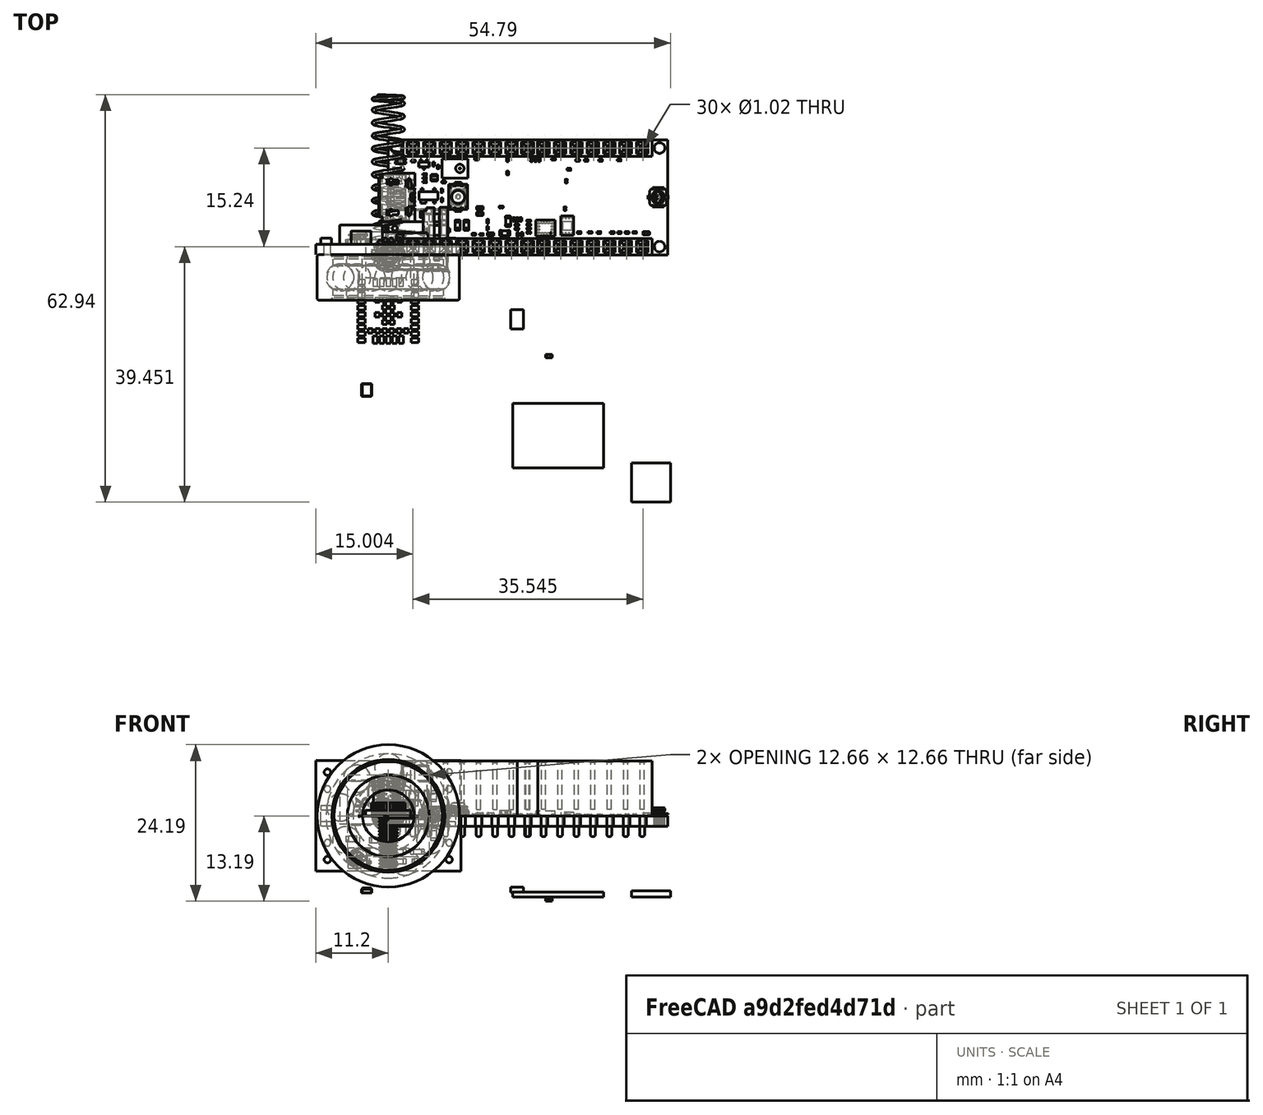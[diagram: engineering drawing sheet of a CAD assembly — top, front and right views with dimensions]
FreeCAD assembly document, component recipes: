
FREECAD ASSEMBLY — COMPONENT RECIPES ("Watch_Winder")

This assembly document has 14 components, labeled P0..P13 below (a component is one placed body or linked part). 4 of them carry a construction recipe — the FreeCAD feature program that regenerates the part from scratch, quoted from this document or its linked companion documents; the rest are supplied as boundary geometry only. No exploded tour is included for this assembly.
COMPONENT P0 — recipe-attached ("Bearing_Stopper001", modeled in this document).
Construction recipe (the document's own serialized feature program — sketch geometry with constraints, then the solid features built on it; lengths are millimeters unless a unit is written):

FEATURE [Sketcher::SketchObject] Sketch021
  ArcFitTolerance = 1e-06
  AttachmentSupport = -> [XZ_Plane150]
  FullyConstrained = true
  MakeInternals = false
  MapMode = 5
  Placement = pos=(0,0,0) rot=(1,0,0;1.5708rad)
  expr: Constraints[16] = 4.2 / 2
  sketch-geometry (6):
    g0: LineSegment StartX=0 StartY=-2.1 StartZ=0 EndX=0 EndY=-8 EndZ=0
    g1: LineSegment StartX=0 StartY=-8 StartZ=0 EndX=-3 EndY=-8 EndZ=0
    g2: LineSegment StartX=-3 StartY=-8 StartZ=0 EndX=-3 EndY=-4 EndZ=0
    g3: LineSegment StartX=-3 StartY=-4 StartZ=0 EndX=-10 EndY=-4 EndZ=0
    g4: LineSegment StartX=-10 StartY=-4 StartZ=0 EndX=-10 EndY=-2.1 EndZ=0
    g5: LineSegment StartX=-10 StartY=-2.1 StartZ=0 EndX=0 EndY=-2.1 EndZ=0
  constraints (18):
    c: PointOnObject(g0,g-2)
    c: Coincident(g1,g0)
    c: Horizontal(g1)
    c: Coincident(g2,g1)
    c: Vertical(g2)
    c: Coincident(g3,g2)
    c: Horizontal(g3)
    c: Coincident(g4,g3)
    c: Vertical(g4)
    c: DistanceX(g3,g3) = 7
    c: DistanceX(g1,g1) = 3
    c: Horizontal(g5)
    c: Coincident(g0,g5)
    c: Coincident(g4,g5)
    c: DistanceY(g3,g-1) = 4
    c: DistanceY(g0,g-1) = 8
    c: DistanceY(g4,g-1) = 2.1
    c: Vertical(g0)
FEATURE [PartDesign::Revolution] Revolution
  Angle = 360
  Angle2 = 60
  Axis = (1,0,0)
  Base = (0,0,0)
  Placement = pos=(0,0,0) rot=(1,0,0;1.5708rad)
  Profile = -> Sketch021
  ReferenceAxis = -> Sketch021 [H_Axis]
  Refine = true
  Reversed = true
  Suppressed = false
  Type = 0
FEATURE [PartDesign::Fillet] Fillet012
  Base = -> Revolution [Edge2]
  BaseFeature = -> Revolution
  Placement = pos=(0,0,0) rot=(1,0,0;1.5708rad)
  Radius = 1
  Refine = true
  SupportTransform = false
  Suppressed = false
  UseAllEdges = false
FEATURE [PartDesign::Body] Body006  label="Bearing_Stopper"
  AllowCompound = false
  Group = -> [Sketch021,Revolution,Fillet012]
  Origin = -> Origin150
  Placement = pos=(-21.5,25.5,-38) rot=(0,0,1;0rad)
  Tip = -> Fillet012
COMPONENT P1 — same part as P0; its construction recipe is shown at P0.
COMPONENT P2 — recipe-attached ("Body009", modeled in this document).
Construction recipe (the document's own serialized feature program — sketch geometry with constraints, then the solid features built on it; lengths are millimeters unless a unit is written):

FEATURE [Sketcher::SketchObject] Sketch011
  ArcFitTolerance = 1e-06
  AttachmentSupport = -> [YZ_Plane005]
  FullyConstrained = true
  MakeInternals = false
  MapMode = 5
  Placement = pos=(0,0,0) rot=(0.57735,0.57735,0.57735;2.0944rad)
  sketch-geometry (7):
    g0: LineSegment StartX=-67.5 StartY=55 StartZ=0 EndX=-67.5 EndY=-55 EndZ=0
    g1: LineSegment StartX=-67.5 StartY=-55 StartZ=0 EndX=42.5 EndY=-55 EndZ=0
    g2: LineSegment StartX=42.5 StartY=-55 StartZ=0 EndX=42.5 EndY=55 EndZ=0
    g3: LineSegment StartX=42.5 StartY=55 StartZ=0 EndX=-67.5 EndY=55 EndZ=0
    g4: LineSegment [constr] StartX=-12.5 StartY=55 StartZ=0 EndX=-12.5 EndY=-55 EndZ=0
    g5: LineSegment [constr] StartX=-67.5 StartY=-7e-16 StartZ=0 EndX=42.5 EndY=7e-16 EndZ=0
    g6: GeomPoint [constr] X=-12.5 Y=0 Z=0
  constraints (17):
    c: Coincident(g0,g1)
    c: Coincident(g1,g2)
    c: Coincident(g2,g3)
    c: Coincident(g3,g0)
    c: Vertical(g0)
    c: Vertical(g2)
    c: Horizontal(g1)
    c: Horizontal(g3)
    c: DistanceX(g3,g3) = 110
    c: DistanceY(g0,g0) = 110
    c: Symmetric(g3,g3,g4)
    c: Symmetric(g1,g1,g4)
    c: Symmetric(g0,g0,g5)
    c: Symmetric(g2,g2,g5)
    c: Symmetric(g5,g5,g6)
    c: DistanceX(g6,g-1) = 12.5
    c: PointOnObject(g6,g-1)
FEATURE [PartDesign::Pad] Pad006  label="Depth"
  Direction = (1,0,0)
  Length = 86
  Length2 = 10
  Placement = pos=(0,0,0) rot=(1,1,1;2.0944rad)
  Profile = -> Sketch011
  ReferenceAxis = -> Sketch011 [N_Axis]
  Refine = true
  Reversed = true
  Suppressed = false
  Type = 0
FEATURE [Sketcher::SketchObject] Sketch012
  ArcFitTolerance = 1e-06
  AttachmentSupport = -> [Pad006]
  ExternalGeometry = -> [Pad006]
  FullyConstrained = true
  MakeInternals = false
  MapMode = 5
  Placement = pos=(0,0,0) rot=(0.57735,0.57735,0.57735;2.0944rad)
  sketch-geometry (4):
    g0: LineSegment [constr] StartX=-67.5 StartY=2.15e-14 StartZ=0 EndX=42.5 EndY=-1.24e-14 EndZ=0
    g1: LineSegment [constr] StartX=-12.5 StartY=-55 StartZ=0 EndX=-12.5 EndY=55 EndZ=0
    g2: GeomPoint [constr] X=-12.5 Y=4.5e-15 Z=0
    g3: Circle CenterX=-12.5 CenterY=4.5e-15 CenterZ=0 NormalX=0 NormalY=0 NormalZ=1 AngleXU=0 Radius=44
  constraints (7):
    c: Symmetric(g-6,g-6,g0)
    c: Symmetric(g-5,g-5,g0)
    c: Symmetric(g-4,g-4,g1)
    c: Symmetric(g-3,g-3,g1)
    c: Symmetric(g0,g0,g2)
    c: Coincident(g3,g2)
    c: Diameter(g3) = 88
FEATURE [PartDesign::Pocket] Pocket005  label="Drum_Cavity"
  BaseFeature = -> Pad006
  Direction = (-1,0,0)
  Length = 58
  Length2 = 5
  Placement = pos=(0,0,0) rot=(1,1,1;2.0944rad)
  Profile = -> Sketch012
  ReferenceAxis = -> Sketch012 [N_Axis]
  Refine = true
  Suppressed = false
  Type = 0
FEATURE [Sketcher::SketchObject] Sketch013
  ArcFitTolerance = 1e-06
  AttachmentSupport = -> [Pocket005]
  ExternalGeometry = -> [Pocket005]
  FullyConstrained = true
  MakeInternals = false
  MapMode = 5
  Placement = pos=(0,0,0) rot=(0.57735,0.57735,0.57735;2.0944rad)
  expr: Constraints[4] = 85 / 2 + 22 / 2
  sketch-geometry (6):
    g0: LineSegment [constr] StartX=-12.5 StartY=8.7e-15 StartZ=0 EndX=42.5 EndY=-55 EndZ=0
    g1: Circle [constr] CenterX=25.3302 CenterY=-37.8302 CenterZ=0 NormalX=0 NormalY=0 NormalZ=1 AngleXU=0 Radius=11
    g2: Circle CenterX=25.3302 CenterY=-37.8302 CenterZ=0 NormalX=0 NormalY=0 NormalZ=1 AngleXU=0 Radius=11.75
    g3: LineSegment [constr] StartX=-12.5 StartY=8.7e-15 StartZ=0 EndX=-67.5 EndY=-55 EndZ=0
    g4: LineSegment [constr] StartX=25.3302 StartY=-37.8302 StartZ=0 EndX=-50.3302 EndY=-37.8302 EndZ=0
    g5: Circle CenterX=-50.3302 CenterY=-37.8302 CenterZ=0 NormalX=0 NormalY=0 NormalZ=1 AngleXU=0 Radius=11.75
  constraints (14):
    c: Coincident(g0,g-3)
    c: Coincident(g0,g-5)
    c: PointOnObject(g1,g0)
    c: Diameter(g1) = 22
    c: Distance(g1,g0) = 53.5
    c: Coincident(g2,g1)
    c: Coincident(g3,g0)
    c: Coincident(g3,g-6)
    c: Coincident(g4,g1)
    c: PointOnObject(g4,g3)
    c: Horizontal(g4)
    c: Coincident(g5,g4)
    c: Equal(g2,g5)
    c: Diameter(g2) = 23.5
FEATURE [PartDesign::Pocket] Pocket006  label="Bearing"
  BaseFeature = -> Pocket005
  Direction = (-1,0,0)
  Length = 31.5
  Length2 = 5
  Placement = pos=(0,0,0) rot=(1,1,1;2.0944rad)
  Profile = -> Sketch013
  ReferenceAxis = -> Sketch013 [N_Axis]
  Refine = true
  Suppressed = false
  Type = 0
  expr: Length = 56 / 2 + 7 / 2
FEATURE [Sketcher::SketchObject] Sketch016
  ArcFitTolerance = 1e-06
  AttachmentSupport = -> [Pocket006]
  ExternalGeometry = -> [Pocket006]
  FullyConstrained = true
  MakeInternals = false
  MapMode = 5
  Placement = pos=(-86,0,0) rot=(0.57735,0.57735,-0.57735;4.18879rad)
  expr: Constraints[20] = 90 - 35
  sketch-geometry (8):
    g0: LineSegment StartX=32.5 StartY=-45 StartZ=0 EndX=32.5 EndY=27 EndZ=0
    g1: LineSegment StartX=-22.5 StartY=45 StartZ=0 EndX=-57.5 EndY=45 EndZ=0
    g2: LineSegment StartX=-57.5 StartY=45 StartZ=0 EndX=-57.5 EndY=-45 EndZ=0
    g3: LineSegment StartX=-57.5 StartY=-45 StartZ=0 EndX=32.5 EndY=-45 EndZ=0
    g4: LineSegment [constr] StartX=-12.5 StartY=-55 StartZ=0 EndX=-12.5 EndY=55 EndZ=0
    g5: LineSegment [constr] StartX=42.5 StartY=4.18e-14 StartZ=0 EndX=-67.5 EndY=0 EndZ=0
    g6: LineSegment StartX=-22.5 StartY=27 StartZ=0 EndX=32.5 EndY=27 EndZ=0
    g7: LineSegment StartX=-22.5 StartY=27 StartZ=0 EndX=-22.5 EndY=45 EndZ=0
  constraints (22):
    c: Coincident(g1,g2)
    c: Coincident(g2,g3)
    c: Coincident(g3,g0)
    c: Vertical(g0)
    c: Vertical(g2)
    c: Horizontal(g1)
    c: Horizontal(g3)
    c: DistanceX(g3,g3) = 90
    c: Symmetric(g-3,g-3,g4)
    c: Symmetric(g-4,g-4,g4)
    c: DistanceX(g2,g4) = 45
    c: Symmetric(g-5,g-5,g5)
    c: Symmetric(g-6,g-6,g5)
    c: DistanceY(g0,g5) = 45
    c: Horizontal(g6)
    c: Coincident(g7,g6)
    c: Vertical(g7)
    c: DistanceY(g2,g2) = 90
    c: Coincident(g0,g6)
    c: Coincident(g1,g7)
    c: DistanceX(g6,g6) = 55
    c: DistanceY(g7,g7) = 18
FEATURE [PartDesign::Pocket] Pocket008  label="Rear_Cavity"
  BaseFeature = -> Pocket006
  Direction = (1,0,0)
  Length = 20
  Length2 = 5
  Placement = pos=(0,0,0) rot=(1,1,1;2.0944rad)
  Profile = -> Sketch016
  ReferenceAxis = -> Sketch016 [N_Axis]
  Refine = true
  Suppressed = false
  Type = 0
FEATURE [Sketcher::SketchObject] Sketch017
  ArcFitTolerance = 1e-06
  AttachmentSupport = -> [Pocket008]
  ExternalGeometry = -> [Pocket008]
  FullyConstrained = false
  MakeInternals = false
  MapMode = 5
  Placement = pos=(-66,0,0) rot=(0.57735,0.57735,-0.57735;4.18879rad)
  sketch-geometry (4):
    g0: LineSegment [constr] StartX=-12.5 StartY=55 StartZ=0 EndX=-12.5 EndY=-20.1023 EndZ=0
    g1: LineSegment [constr] StartX=-67.5 StartY=-6.03e-14 StartZ=0 EndX=21.0372 EndY=-6.03e-14 EndZ=0
    g2: GeomPoint [constr] X=-12.5 Y=0 Z=0
    g3: Circle CenterX=-12.5 CenterY=0 CenterZ=0 NormalX=0 NormalY=0 NormalZ=1 AngleXU=0 Radius=12
  constraints (8):
    c: Symmetric(g-3,g-3,g0)
    c: Vertical(g0)
    c: Symmetric(g-4,g-4,g1)
    c: Horizontal(g1)
    c: PointOnObject(g2,g0)
    c: PointOnObject(g2,g1)
    c: Coincident(g3,g2)
    c: Diameter(g3) = 24
FEATURE [PartDesign::Pocket] Pocket009  label="Motor_pass_through"
  BaseFeature = -> Pocket008
  Direction = (1,0,0)
  Length = 5
  Length2 = 5
  Placement = pos=(0,0,0) rot=(1,1,1;2.0944rad)
  Profile = -> Sketch017
  ReferenceAxis = -> Sketch017 [N_Axis]
  Refine = true
  Suppressed = false
  Type = 1
FEATURE [Sketcher::SketchObject] Sketch018
  ArcFitTolerance = 1e-06
  AttachmentSupport = -> [Pocket009]
  ExternalGeometry = -> [Pocket009]
  FullyConstrained = true
  MakeInternals = false
  MapMode = 5
  Placement = pos=(-66,0,0) rot=(0.57735,0.57735,-0.57735;4.18879rad)
  expr: Constraints[5] = 35 / 2
  sketch-geometry (3):
    g0: Circle CenterX=-30 CenterY=8 CenterZ=0 NormalX=0 NormalY=0 NormalZ=1 AngleXU=0 Radius=2
    g1: Circle CenterX=5 CenterY=8 CenterZ=0 NormalX=0 NormalY=0 NormalZ=1 AngleXU=0 Radius=2
    g2: LineSegment [constr] StartX=-30 StartY=8 StartZ=0 EndX=5 EndY=8 EndZ=0
  constraints (8):
    c: Coincident(g2,g0)
    c: Coincident(g2,g1)
    c: Horizontal(g2)
    c: DistanceX(g2,g2) = 35
    c: DistanceY(g-3,g1) = 8
    c: DistanceX(g-3,g1) = 17.5
    c: Equal(g0,g1)
    c: Diameter(g0) = 4
FEATURE [PartDesign::Pocket] Pocket010  label="Motor_fix"
  BaseFeature = -> Pocket009
  Direction = (1,0,0)
  Length = 6.74
  Length2 = 5
  Placement = pos=(0,0,0) rot=(1,1,1;2.0944rad)
  Profile = -> Sketch018
  ReferenceAxis = -> Sketch018 [N_Axis]
  Refine = true
  Suppressed = false
  Type = 0
FEATURE [Sketcher::SketchObject] Sketch019
  ArcFitTolerance = 1e-06
  AttachmentSupport = -> [Pocket010]
  ExternalGeometry = -> [Pocket010]
  FullyConstrained = true
  MakeInternals = false
  MapMode = 5
  Placement = pos=(-66,0,0) rot=(0.57735,0.57735,-0.57735;4.18879rad)
  expr: Constraints[45] = 35 / 2
  expr: Constraints[46] = 18 / 2
  expr: Constraints[47] = 44 / 2
  expr: Constraints[54] = 17 / 2
  expr: Constraints[55] = (22 - 10) / 2
  sketch-geometry (23):
    g0: LineSegment [constr] StartX=-54.6 StartY=-42.3 StartZ=0 EndX=-28 EndY=-42.3 EndZ=0
    g1: LineSegment [constr] StartX=-28 StartY=-42.3 StartZ=0 EndX=-28 EndY=-12.7 EndZ=0
    g2: LineSegment [constr] StartX=-28 StartY=-12.7 StartZ=0 EndX=-54.6 EndY=-12.7 EndZ=0
    g3: LineSegment [constr] StartX=-54.6 StartY=-12.7 StartZ=0 EndX=-54.6 EndY=-42.3 EndZ=0
    g4: LineSegment [constr] StartX=-41.3 StartY=-12.7 StartZ=0 EndX=-41.3 EndY=-42.3 EndZ=0
    g5: LineSegment [constr] StartX=-54.6 StartY=-27.5 StartZ=0 EndX=-28 EndY=-27.5 EndZ=0
    g6: Circle CenterX=-54.6 CenterY=-12.7 CenterZ=0 NormalX=0 NormalY=0 NormalZ=1 AngleXU=0 Radius=2
    g7: Circle CenterX=-28 CenterY=-12.7 CenterZ=0 NormalX=0 NormalY=0 NormalZ=1 AngleXU=0 Radius=2
    g8: Circle CenterX=-28 CenterY=-42.3 CenterZ=0 NormalX=0 NormalY=0 NormalZ=1 AngleXU=0 Radius=2
    g9: Circle CenterX=-54.6 CenterY=-42.3 CenterZ=0 NormalX=0 NormalY=0 NormalZ=1 AngleXU=0 Radius=2
    g10: Circle CenterX=15.88 CenterY=-43.32 CenterZ=0 NormalX=0 NormalY=0 NormalZ=1 AngleXU=0 Radius=1.125
    g11: LineSegment [constr] StartX=15.88 StartY=-43.32 StartZ=0 EndX=31.12 EndY=-43.32 EndZ=0
    g12: LineSegment [constr] StartX=31.12 StartY=-43.32 StartZ=0 EndX=31.12 EndY=-2.68 EndZ=0
    g13: LineSegment [constr] StartX=31.12 StartY=-2.68 StartZ=0 EndX=15.88 EndY=-2.68 EndZ=0
    g14: LineSegment [constr] StartX=15.88 StartY=-2.68 StartZ=0 EndX=15.88 EndY=-43.32 EndZ=0
    g15: LineSegment [constr] StartX=23.5 StartY=-2.68 StartZ=0 EndX=23.5 EndY=-43.32 EndZ=0
    g16: LineSegment [constr] StartX=15.88 StartY=-23 StartZ=0 EndX=31.12 EndY=-23 EndZ=0
    g17: Circle CenterX=15.88 CenterY=-2.68 CenterZ=0 NormalX=0 NormalY=0 NormalZ=1 AngleXU=0 Radius=1.125
    g18: Circle CenterX=31.12 CenterY=-2.68 CenterZ=0 NormalX=0 NormalY=0 NormalZ=1 AngleXU=0 Radius=1.125
    g19: Circle CenterX=31.12 CenterY=-43.32 CenterZ=0 NormalX=0 NormalY=0 NormalZ=1 AngleXU=0 Radius=1.125
    g20: Circle CenterX=-49 CenterY=39 CenterZ=0 NormalX=0 NormalY=0 NormalZ=1 AngleXU=0 Radius=2
    g21: Circle CenterX=-49 CenterY=29 CenterZ=0 NormalX=0 NormalY=0 NormalZ=1 AngleXU=0 Radius=2
    g22: LineSegment [constr] StartX=-49 StartY=39 StartZ=0 EndX=-49 EndY=29 EndZ=0
  constraints (56):
    c: Coincident(g0,g1)
    c: Coincident(g1,g2)
    c: Coincident(g2,g3)
    c: Coincident(g3,g0)
    c: Horizontal(g0)
    c: Horizontal(g2)
    c: Vertical(g1)
    c: Vertical(g3)
    c: DistanceX(g0,g0) = 26.6
    c: DistanceY(g3,g3) = 29.6
    c: Symmetric(g2,g2,g4)
    c: Symmetric(g0,g0,g4)
    c: Symmetric(g3,g3,g5)
    c: Symmetric(g1,g1,g5)
    c: Coincident(g6,g2)
    c: Coincident(g7,g1)
    c: Coincident(g8,g0)
    c: Coincident(g9,g0)
    c: Equal(g9,g6)
    c: Equal(g9,g7)
    c: Equal(g9,g8)
    c: Diameter(g9) = 4
    c: Coincident(g11,g12)
    c: Coincident(g12,g13)
    c: Coincident(g13,g14)
    c: Coincident(g14,g11)
    c: Horizontal(g11)
    c: Horizontal(g13)
    c: Vertical(g12)
    c: Vertical(g14)
    c: Coincident(g11,g10)
    c: Symmetric(g13,g13,g15)
    c: Symmetric(g11,g11,g15)
    c: Symmetric(g14,g14,g16)
    c: Symmetric(g12,g12,g16)
    c: Coincident(g17,g13)
    c: Coincident(g18,g12)
    c: Coincident(g19,g11)
    c: Equal(g17,g18)
    c: Equal(g17,g19)
    c: Equal(g17,g10)
    c: Diameter(g17) = 2.25
    c: DistanceY(g15,g15) = 40.64
    c: DistanceX(g16,g16) = 15.24
    c: DistanceX(g-4,g4) = 16.2
    c: DistanceY(g-4,g5) = 17.5
    c: DistanceX(g15,g-4) = 9
    c: DistanceY(g-4,g16) = 22
    c: Coincident(g22,g20)
    c: Coincident(g22,g21)
    c: Vertical(g22)
    c: Equal(g20,g21)
    c: Diameter(g20) = 4
    c: DistanceY(g22,g22) = 10
    c: DistanceX(g-5,g20) = 8.5
    c: DistanceY(g20,g-5) = 6
FEATURE [Sketcher::SketchObject] Sketch020
  ArcFitTolerance = 1e-06
  FullyConstrained = true
  MakeInternals = false
  MapMode = 5
  Placement = pos=(-31.5,3.5e-14,-1.75e-14) rot=(0.57735,0.57735,0.57735;2.0944rad)
  sketch-geometry (2):
    g0: Circle CenterX=-50.3302 CenterY=-37.8302 CenterZ=0 NormalX=0 NormalY=0 NormalZ=1 AngleXU=0 Radius=2.8
    g1: Circle CenterX=25.3302 CenterY=-37.8302 CenterZ=0 NormalX=0 NormalY=0 NormalZ=1 AngleXU=0 Radius=2.8
  constraints (4):
    c: Coincident(g0,g-3)
    c: Coincident(g1,g-4)
    c: Equal(g1,g0)
    c: Diameter(g1) = 5.6
FEATURE [PartDesign::Pocket] Pocket012  label="Bearing_stopper"
  BaseFeature = -> Pocket010
  Direction = (-1,1.1e-15,0)
  Length = 9.55
  Length2 = 5
  Placement = pos=(0,0,0) rot=(1,1,1;2.0944rad)
  Profile = -> Sketch020
  ReferenceAxis = -> Sketch020 [N_Axis]
  Refine = true
  Suppressed = false
  Type = 0
  expr: Length = 8.15 + 0.7 * 2
FEATURE [PartDesign::Pad] Pad008  label="PCBs_Stand"
  BaseFeature = -> Pocket012
  Direction = (-1,0,0)
  Length = 2
  Length2 = 10
  Placement = pos=(0,0,0) rot=(1,1,1;2.0944rad)
  Profile = -> Sketch019
  ReferenceAxis = -> Sketch019 [N_Axis]
  Refine = true
  Suppressed = false
  Type = 0
FEATURE [Sketcher::SketchObject] Sketch022
  ArcFitTolerance = 1e-06
  AttachmentSupport = -> [Pad008]
  ExternalGeometry = -> [Pad008]
  FullyConstrained = true
  MakeInternals = false
  MapMode = 5
  Placement = pos=(-68,0,0) rot=(0.57735,0.57735,-0.57735;4.18879rad)
  sketch-geometry (8):
    g0: Circle CenterX=-54.6 CenterY=-12.7 CenterZ=0 NormalX=0 NormalY=0 NormalZ=1 AngleXU=0 Radius=1.375
    g1: Circle CenterX=-54.6 CenterY=-42.3 CenterZ=0 NormalX=0 NormalY=0 NormalZ=1 AngleXU=0 Radius=1.375
    g2: Circle CenterX=-28 CenterY=-12.7 CenterZ=0 NormalX=0 NormalY=0 NormalZ=1 AngleXU=0 Radius=1.375
    g3: Circle CenterX=-28 CenterY=-42.3 CenterZ=0 NormalX=0 NormalY=0 NormalZ=1 AngleXU=0 Radius=1.375
    g4: Circle CenterX=15.88 CenterY=-2.68 CenterZ=0 NormalX=0 NormalY=0 NormalZ=1 AngleXU=0 Radius=0.625
    g5: Circle CenterX=31.12 CenterY=-2.68 CenterZ=0 NormalX=0 NormalY=0 NormalZ=1 AngleXU=0 Radius=0.625
    g6: Circle CenterX=15.88 CenterY=-43.32 CenterZ=0 NormalX=0 NormalY=0 NormalZ=1 AngleXU=0 Radius=0.625
    g7: Circle CenterX=31.12 CenterY=-43.32 CenterZ=0 NormalX=0 NormalY=0 NormalZ=1 AngleXU=0 Radius=0.625
  constraints (16):
    c: Coincident(g0,g-3)
    c: Coincident(g1,g-5)
    c: Coincident(g2,g-4)
    c: Coincident(g3,g-6)
    c: Coincident(g4,g-7)
    c: Coincident(g5,g-8)
    c: Coincident(g6,g-10)
    c: Coincident(g7,g-9)
    c: Equal(g6,g7)
    c: Equal(g6,g5)
    c: Equal(g6,g4)
    c: Diameter(g6) = 1.25
    c: Equal(g0,g2)
    c: Equal(g0,g3)
    c: Equal(g0,g1)
    c: Diameter(g0) = 2.75
FEATURE [PartDesign::Pad] Pad009  label="PCBs_Pins"
  BaseFeature = -> Pad008
  Direction = (-1,0,0)
  Length = 1
  Length2 = 10
  Placement = pos=(0,0,0) rot=(1,1,1;2.0944rad)
  Profile = -> Sketch022
  ReferenceAxis = -> Sketch022 [N_Axis]
  Refine = true
  Suppressed = false
  Type = 0
FEATURE [Sketcher::SketchObject] Sketch023
  ArcFitTolerance = 1e-06
  AttachmentSupport = -> [Pad009]
  ExternalGeometry = -> [Pad009]
  FullyConstrained = true
  MakeInternals = false
  MapMode = 5
  Placement = pos=(-86,0,0) rot=(0.57735,0.57735,-0.57735;4.18879rad)
  sketch-geometry (11):
    g0: LineSegment [constr] StartX=-12.5 StartY=45 StartZ=0 EndX=-7.5 EndY=44.5 EndZ=0
    g1: LineSegment StartX=-7.5 StartY=44.5 StartZ=0 EndX=42.5 EndY=44.5 EndZ=0
    g2: LineSegment [constr] StartX=-22.5 StartY=45 StartZ=0 EndX=-12.5 EndY=45 EndZ=0
    g3: LineSegment [constr] StartX=-12.5 StartY=45 StartZ=0 EndX=-12.5 EndY=31 EndZ=0
    g4: LineSegment [constr] StartX=-22.5 StartY=45 StartZ=0 EndX=-22.5 EndY=27 EndZ=0
    g5: LineSegment [constr] StartX=-12.5 StartY=31 StartZ=0 EndX=-22.5 EndY=31 EndZ=0
    g6: LineSegment StartX=-7.5 StartY=44.5 StartZ=0 EndX=-7.5 EndY=31.5 EndZ=0
    g7: LineSegment [constr] StartX=-12.5 StartY=31 StartZ=0 EndX=-7.5 EndY=31.5 EndZ=0
    g8: LineSegment StartX=-7.5 StartY=31.5 StartZ=0 EndX=42.5 EndY=31.5 EndZ=0
    g9: LineSegment StartX=42.5 StartY=31.5 StartZ=0 EndX=42.5 EndY=44.5 EndZ=0
    g10: LineSegment [constr] StartX=-12.5 StartY=38 StartZ=0 EndX=-7.5 EndY=38 EndZ=0
  constraints (29):
    c: Coincident(g1,g0)
    c: PointOnObject(g1,g-5)
    c: Horizontal(g1)
    c: DistanceX(g-3,g0) = 10
    c: Coincident(g2,g-3)
    c: Coincident(g2,g0)
    c: Horizontal(g2)
    c: Coincident(g3,g0)
    c: Vertical(g3)
    c: Coincident(g4,g2)
    c: Coincident(g4,g-4)
    c: Coincident(g5,g3)
    c: PointOnObject(g5,g4)
    c: Horizontal(g5)
    c: Coincident(g6,g0)
    c: Vertical(g6)
    c: Coincident(g7,g3)
    c: Coincident(g7,g6)
    c: Coincident(g8,g6)
    c: PointOnObject(g8,g-5)
    c: Horizontal(g8)
    c: Coincident(g9,g8)
    c: Coincident(g9,g1)
    c: DistanceY(g3,g3) = 14
    c: DistanceX(g2,g0) = 15
    c: DistanceY(g6,g6) = 13
    c: Symmetric(g3,g3,g10)
    c: Symmetric(g6,g6,g10)
    c: Horizontal(g10)
FEATURE [PartDesign::Pocket] Pocket013  label="DC_Open"
  BaseFeature = -> Pad009
  Direction = (1,-1.9e-15,1e-16)
  Length = 20
  Length2 = 5
  Placement = pos=(0,0,0) rot=(1,1,1;2.0944rad)
  Profile = -> Sketch023
  ReferenceAxis = -> Sketch023 [N_Axis]
  Refine = true
  Suppressed = false
  Type = 0
FEATURE [Sketcher::SketchObject] Sketch024
  ArcFitTolerance = 1e-06
  AttachmentSupport = -> [Pocket013]
  ExternalGeometry = -> [Pocket013]
  FullyConstrained = true
  MakeInternals = false
  MapMode = 5
  Placement = pos=(-66,0,0) rot=(0.57735,0.57735,-0.57735;4.18879rad)
  sketch-geometry (8):
    g0: LineSegment StartX=-22.5 StartY=45 StartZ=0 EndX=-22.5 EndY=31 EndZ=0
    g1: LineSegment StartX=-22.5 StartY=31 StartZ=0 EndX=-12.5 EndY=31 EndZ=0
    g2: LineSegment StartX=-22.5 StartY=45 StartZ=0 EndX=-12.5 EndY=45 EndZ=0
    g3: LineSegment [constr] StartX=-12.5 StartY=45 StartZ=0 EndX=-12.5 EndY=31 EndZ=0
    g4: LineSegment StartX=-12.5 StartY=45 StartZ=0 EndX=-7.5 EndY=44.5 EndZ=0
    g5: LineSegment StartX=-12.5 StartY=31 StartZ=0 EndX=-7.5 EndY=31.5 EndZ=0
    g6: LineSegment [constr] StartX=-12.5 StartY=38 StartZ=0 EndX=-7.5 EndY=38 EndZ=0
    g7: LineSegment StartX=-7.5 StartY=44.5 StartZ=0 EndX=-7.5 EndY=31.5 EndZ=0
  constraints (20):
    c: Coincident(g0,g-3)
    c: Vertical(g0)
    c: Coincident(g1,g0)
    c: Horizontal(g1)
    c: Coincident(g2,g0)
    c: Horizontal(g2)
    c: Coincident(g3,g2)
    c: Coincident(g3,g1)
    c: Vertical(g3)
    c: Coincident(g4,g2)
    c: Coincident(g4,g-5)
    c: Coincident(g5,g1)
    c: Coincident(g5,g-5)
    c: Symmetric(g3,g3,g6)
    c: Symmetric(g-5,g-5,g6)
    c: Horizontal(g6)
    c: DistanceX(g0,g2) = 10
    c: DistanceY(g-5,g-5) = 13
    c: Coincident(g7,g4)
    c: Coincident(g7,g5)
FEATURE [PartDesign::Pocket] Pocket014  label="DC_Hole"
  BaseFeature = -> Pocket013
  Direction = (1,-1.4e-15,1e-16)
  Length = 11.5
  Length2 = 5
  Placement = pos=(0,0,0) rot=(1,1,1;2.0944rad)
  Profile = -> Sketch024
  ReferenceAxis = -> Sketch024 [N_Axis]
  Refine = true
  Reversed = true
  Suppressed = false
  Type = 0
FEATURE [Sketcher::SketchObject] Sketch025
  ArcFitTolerance = 1e-06
  AttachmentSupport = -> [Pocket014]
  ExternalGeometry = -> [Pocket014]
  FullyConstrained = true
  MakeInternals = false
  MapMode = 5
  Placement = pos=(-66,0,-1.478e-13) rot=(0.57735,0.57735,-0.57735;4.18879rad)
  sketch-geometry (12):
    g0: LineSegment StartX=-57.5 StartY=23.25 StartZ=0 EndX=-57.5 EndY=21.25 EndZ=0
    g1: LineSegment StartX=-57.5 StartY=21.25 StartZ=0 EndX=-40.5 EndY=21.25 EndZ=0
    g2: LineSegment StartX=-40.5 StartY=21.25 StartZ=0 EndX=-40.5 EndY=23.25 EndZ=0
    g3: LineSegment StartX=-40.5 StartY=23.25 StartZ=0 EndX=-57.5 EndY=23.25 EndZ=0
    g4: LineSegment StartX=12.75 StartY=-45 StartZ=0 EndX=12.75 EndY=-1 EndZ=0
    g5: LineSegment StartX=12.75 StartY=-1 StartZ=0 EndX=14.75 EndY=-1 EndZ=0
    g6: LineSegment StartX=14.75 StartY=-1 StartZ=0 EndX=14.75 EndY=-45 EndZ=0
    g7: LineSegment StartX=14.75 StartY=-45 StartZ=0 EndX=12.75 EndY=-45 EndZ=0
    g8: LineSegment StartX=-57.5 StartY=-10.25 StartZ=0 EndX=-25.5 EndY=-10.25 EndZ=0
    g9: LineSegment StartX=-25.5 StartY=-10.25 StartZ=0 EndX=-25.5 EndY=-8.25 EndZ=0
    g10: LineSegment StartX=-25.5 StartY=-8.25 StartZ=0 EndX=-57.5 EndY=-8.25 EndZ=0
    g11: LineSegment StartX=-57.5 StartY=-8.25 StartZ=0 EndX=-57.5 EndY=-10.25 EndZ=0
  constraints (36):
    c: Coincident(g0,g1)
    c: Coincident(g1,g2)
    c: Coincident(g2,g3)
    c: Coincident(g3,g0)
    c: Vertical(g0)
    c: Vertical(g2)
    c: Horizontal(g1)
    c: Horizontal(g3)
    c: PointOnObject(g0,g-3)
    c: DistanceY(g0,g-3) = 21.75
    c: DistanceY(g0,g0) = 2
    c: DistanceX(g1,g1) = 17
    c: Coincident(g4,g5)
    c: Coincident(g5,g6)
    c: Coincident(g6,g7)
    c: Coincident(g7,g4)
    c: Vertical(g4)
    c: Vertical(g6)
    c: Horizontal(g5)
    c: Horizontal(g7)
    c: PointOnObject(g4,g-5)
    c: DistanceY(g6,g6) = 44
    c: DistanceX(g4,g6) = 2
    c: DistanceX(g6,g-5) = 17.75
    c: Coincident(g8,g9)
    c: Coincident(g9,g10)
    c: Coincident(g10,g11)
    c: Coincident(g11,g8)
    c: Horizontal(g8)
    c: Horizontal(g10)
    c: Vertical(g9)
    c: Vertical(g11)
    c: PointOnObject(g8,g-3)
    c: DistanceY(g8,g10) = 2
    c: DistanceY(g-5,g8) = 34.75
    c: DistanceX(g10,g10) = 32
FEATURE [PartDesign::Pad] Pad010  label="PCB_Slots"
  BaseFeature = -> Pocket014
  Direction = (-1,0,-2.2e-15)
  Length = 1
  Length2 = 10
  Placement = pos=(0,0,0) rot=(1,1,1;2.0944rad)
  Profile = -> Sketch025
  ReferenceAxis = -> Sketch025 [N_Axis]
  Refine = true
  Suppressed = false
  Type = 0
FEATURE [Sketcher::SketchObject] Sketch026
  ArcFitTolerance = 1e-06
  AttachmentSupport = -> [Pad010]
  ExternalGeometry = -> [Pad010]
  FullyConstrained = true
  MakeInternals = false
  MapMode = 5
  Placement = pos=(-2.2e-15,2e-16,1) rot=(0.707107,0.707107,0;3.14159rad)
  sketch-geometry (8):
    g0: LineSegment StartX=14.75 StartY=-67 StartZ=0 EndX=12.75 EndY=-67 EndZ=0
    g1: LineSegment StartX=12.75 StartY=-67 StartZ=0 EndX=12.75 EndY=-71 EndZ=0
    g2: LineSegment StartX=12.75 StartY=-71 StartZ=0 EndX=14.75 EndY=-71 EndZ=0
    g3: LineSegment [constr] StartX=14.75 StartY=-71 StartZ=0 EndX=14.75 EndY=-67 EndZ=0
    g4: LineSegment StartX=14 StartY=-70 StartZ=0 EndX=14 EndY=-68 EndZ=0
    g5: LineSegment [constr] StartX=14 StartY=-69 StartZ=0 EndX=12.75 EndY=-69 EndZ=0
    g6: ArcOfCircle CenterX=13.7083 CenterY=-71 CenterZ=0 NormalX=0 NormalY=0 NormalZ=1 AngleXU=0 Radius=1.04167 StartAngle=1.33e-14 EndAngle=1.287
    g7: ArcOfCircle CenterX=13.7083 CenterY=-67 CenterZ=0 NormalX=0 NormalY=0 NormalZ=1 AngleXU=0 Radius=1.04167 StartAngle=4.99618 EndAngle=6.28319
  constraints (22):
    c: Coincident(g0,g-3)
    c: Coincident(g0,g-3)
    c: Distance(g1) = 4
    c: Coincident(g1,g0)
    c: Vertical(g1)
    c: Coincident(g2,g1)
    c: Horizontal(g2)
    c: Coincident(g3,g2)
    c: Coincident(g3,g0)
    c: Vertical(g3)
    c: Vertical(g4)
    c: DistanceY(g4,g4) = 2
    c: Symmetric(g4,g4,g5)
    c: Symmetric(g1,g1,g5)
    c: Horizontal(g5)
    c: DistanceX(g4,g2) = 0.75
    c: Coincident(g6,g2)
    c: Coincident(g6,g4)
    c: Coincident(g7,g0)
    c: Coincident(g7,g4)
    c: Perpendicular(g7,g0)
    c: Perpendicular(g6,g2)
FEATURE [PartDesign::Pad] Pad011  label="Arduino_Slot"
  BaseFeature = -> Pad010
  Direction = (2.3e-15,0,-1)
  Length = 44
  Length2 = 10
  Placement = pos=(0,0,0) rot=(1,1,1;2.0944rad)
  Profile = -> Sketch026
  ReferenceAxis = -> Sketch026 [N_Axis]
  Refine = true
  Reversed = true
  Suppressed = false
  Type = 0
FEATURE [Sketcher::SketchObject] Sketch028
  ArcFitTolerance = 1e-06
  AttachmentSupport = -> [Pad011]
  ExternalGeometry = -> [Pad011]
  FullyConstrained = true
  MakeInternals = false
  MapMode = 5
  Placement = pos=(-5.6e-15,-25.5,0) rot=(0.57735,0.57735,0.57735;4.18879rad)
  sketch-geometry (8):
    g0: LineSegment StartX=10.25 StartY=-67 StartZ=0 EndX=8.25 EndY=-67 EndZ=0
    g1: LineSegment StartX=8.25 StartY=-67 StartZ=0 EndX=8.25 EndY=-71 EndZ=0
    g2: LineSegment StartX=8.25 StartY=-71 StartZ=0 EndX=10.25 EndY=-71 EndZ=0
    g3: LineSegment [constr] StartX=10.25 StartY=-71 StartZ=0 EndX=10.25 EndY=-67 EndZ=0
    g4: LineSegment StartX=9.5 StartY=-70 StartZ=0 EndX=9.5 EndY=-68 EndZ=0
    g5: LineSegment [constr] StartX=9.5 StartY=-69 StartZ=0 EndX=8.25 EndY=-69 EndZ=0
    g6: ArcOfCircle CenterX=9.20833 CenterY=-67 CenterZ=0 NormalX=0 NormalY=0 NormalZ=1 AngleXU=0 Radius=1.04167 StartAngle=4.99618 EndAngle=6.28319
    g7: ArcOfCircle CenterX=9.20833 CenterY=-71 CenterZ=0 NormalX=0 NormalY=0 NormalZ=1 AngleXU=0 Radius=1.04167 StartAngle=3.92e-14 EndAngle=1.287
  constraints (22):
    c: Coincident(g0,g-3)
    c: Coincident(g0,g-3)
    c: Distance(g1) = 4
    c: Coincident(g1,g0)
    c: Vertical(g1)
    c: Coincident(g2,g1)
    c: Horizontal(g2)
    c: Coincident(g3,g2)
    c: Coincident(g3,g0)
    c: Vertical(g3)
    c: Distance(g4) = 2
    c: Vertical(g4)
    c: Symmetric(g4,g4,g5)
    c: Symmetric(g1,g1,g5)
    c: Horizontal(g5)
    c: DistanceX(g4,g2) = 0.75
    c: Coincident(g6,g4)
    c: Coincident(g6,g0)
    c: Coincident(g7,g2)
    c: Coincident(g7,g4)
    c: Perpendicular(g6,g0)
    c: Perpendicular(g7,g2)
FEATURE [PartDesign::Pad] Pad012  label="ULN2003_Slot"
  BaseFeature = -> Pad011
  Direction = (0,1,0)
  Length = 32
  Length2 = 10
  Placement = pos=(0,0,0) rot=(1,1,1;2.0944rad)
  Profile = -> Sketch028
  ReferenceAxis = -> Sketch028 [N_Axis]
  Refine = true
  Reversed = true
  Suppressed = false
  Type = 0
FEATURE [Sketcher::SketchObject] Sketch029
  ArcFitTolerance = 1e-06
  AttachmentSupport = -> [Pad012]
  ExternalGeometry = -> [Pad012]
  FullyConstrained = true
  MakeInternals = false
  MapMode = 5
  Placement = pos=(-8.9e-15,-40.5,0) rot=(0.57735,0.57735,0.57735;4.18879rad)
  sketch-geometry (8):
    g0: LineSegment StartX=-23.25 StartY=-67 StartZ=0 EndX=-21.25 EndY=-67 EndZ=0
    g1: LineSegment StartX=-21.25 StartY=-67 StartZ=0 EndX=-21.25 EndY=-71 EndZ=0
    g2: LineSegment StartX=-21.25 StartY=-71 StartZ=0 EndX=-23.25 EndY=-71 EndZ=0
    g3: LineSegment [constr] StartX=-23.25 StartY=-67 StartZ=0 EndX=-23.25 EndY=-71 EndZ=0
    g4: LineSegment StartX=-22.5 StartY=-70 StartZ=0 EndX=-22.5 EndY=-68 EndZ=0
    g5: LineSegment [constr] StartX=-22.5 StartY=-69 StartZ=0 EndX=-21.25 EndY=-69 EndZ=0
    g6: ArcOfCircle CenterX=-22.2083 CenterY=-71 CenterZ=0 NormalX=0 NormalY=0 NormalZ=1 AngleXU=0 Radius=1.04167 StartAngle=1.85459 EndAngle=3.14159
    g7: ArcOfCircle CenterX=-22.2083 CenterY=-67 CenterZ=0 NormalX=0 NormalY=0 NormalZ=1 AngleXU=0 Radius=1.04167 StartAngle=3.14159 EndAngle=4.42859
  constraints (22):
    c: Coincident(g0,g-3)
    c: Coincident(g0,g-3)
    c: Distance(g1) = 4
    c: Coincident(g1,g0)
    c: Vertical(g1)
    c: Coincident(g2,g1)
    c: Horizontal(g2)
    c: Coincident(g3,g0)
    c: Coincident(g3,g2)
    c: Vertical(g3)
    c: Vertical(g4)
    c: DistanceY(g4,g4) = 2
    c: Symmetric(g4,g4,g5)
    c: Symmetric(g1,g1,g5)
    c: Horizontal(g5)
    c: DistanceX(g2,g4) = 0.75
    c: Coincident(g6,g2)
    c: Coincident(g6,g4)
    c: Coincident(g7,g0)
    c: Coincident(g7,g4)
    c: Perpendicular(g6,g2)
    c: Perpendicular(g7,g0)
FEATURE [PartDesign::Pad] Pad013  label="MP1584_Slot"
  BaseFeature = -> Pad012
  Direction = (0,1,0)
  Length = 17
  Length2 = 10
  Placement = pos=(0,0,0) rot=(1,1,1;2.0944rad)
  Profile = -> Sketch029
  ReferenceAxis = -> Sketch029 [N_Axis]
  Refine = true
  Reversed = true
  Suppressed = false
  Type = 0
FEATURE [PartDesign::Fillet] Fillet013
  Base = -> Pad013 [Edge193,Edge191,Edge197,Edge195,Edge199,Edge203,Edge205,Edge201]
  BaseFeature = -> Pad013
  Placement = pos=(0,0,0) rot=(1,1,1;2.0944rad)
  Radius = 0.6
  Refine = true
  SupportTransform = false
  Suppressed = false
  UseAllEdges = false
FEATURE [PartDesign::Fillet] Fillet014
  Base = -> Fillet013 [Edge41,Edge137,Edge177]
  BaseFeature = -> Fillet013
  Placement = pos=(0,0,0) rot=(1,1,1;2.0944rad)
  Radius = 1.5
  Refine = true
  SupportTransform = false
  Suppressed = false
  UseAllEdges = false
FEATURE [PartDesign::Fillet] Fillet015
  Base = -> Fillet014 [Edge47,Edge42,Edge60,Edge55,Edge59]
  BaseFeature = -> Fillet014
  Placement = pos=(0,0,0) rot=(1,1,1;2.0944rad)
  Radius = 1
  Refine = true
  SupportTransform = false
  Suppressed = false
  UseAllEdges = false
FEATURE [PartDesign::Fillet] Fillet016
  Base = -> Fillet015 [Edge32,Edge33,Edge35,Edge34,Edge39,Edge37,Edge38,Edge40]
  BaseFeature = -> Fillet015
  Placement = pos=(0,0,0) rot=(1,1,1;2.0944rad)
  Radius = 0.75
  Refine = true
  SupportTransform = false
  Suppressed = false
  UseAllEdges = false
FEATURE [Sketcher::SketchObject] Sketch030
  ArcFitTolerance = 1e-06
  AttachmentSupport = -> [Fillet016]
  ExternalGeometry = -> [Fillet016]
  FullyConstrained = false
  MakeInternals = false
  MapMode = 5
  Placement = pos=(-31.5,0,0) rot=(0.57735,0.57735,0.57735;2.0944rad)
  sketch-geometry (4):
    g0: Circle CenterX=-50.3302 CenterY=-37.8302 CenterZ=0 NormalX=0 NormalY=0 NormalZ=1 AngleXU=0 Radius=6
    g1: Circle CenterX=25.3302 CenterY=-37.8302 CenterZ=0 NormalX=0 NormalY=0 NormalZ=1 AngleXU=0 Radius=6
    g2: Circle CenterX=-50.3302 CenterY=-37.8302 CenterZ=0 NormalX=0 NormalY=0 NormalZ=1 AngleXU=0 Radius=2
    g3: Circle CenterX=25.3302 CenterY=-37.8302 CenterZ=0 NormalX=0 NormalY=0 NormalZ=1 AngleXU=0 Radius=2
  constraints (6):
    c: Coincident(g0,g-3)
    c: Coincident(g1,g-4)
    c: Equal(g1,g0)
    c: Diameter(g1) = 12
    c: Coincident(g2,g0)
    c: Coincident(g3,g1)
FEATURE [PartDesign::Pad] Pad014  label="Bearing_Separator"
  BaseFeature = -> Fillet016
  Direction = (1,0,0)
  Length = 3
  Length2 = 10
  Placement = pos=(0,0,0) rot=(1,1,1;2.0944rad)
  Profile = -> Sketch030
  ReferenceAxis = -> Sketch030 [N_Axis]
  Refine = true
  Suppressed = false
  Type = 0
FEATURE [Sketcher::SketchObject] Sketch040
  ArcFitTolerance = 1e-06
  FullyConstrained = true
  MakeInternals = false
  MapMode = 5
  Placement = pos=(1.441e-13,-3.289e-13,-55) rot=(0.707107,0.707107,0;3.14159rad)
  sketch-geometry (13):
    g0: LineSegment StartX=41.5 StartY=-2 StartZ=0 EndX=40.6414 EndY=-1.14142 EndZ=0
    g1: LineSegment StartX=40.6414 StartY=-0.858579 StartZ=0 EndX=41.1586 EndY=-0.341421 EndZ=0
    g2: LineSegment StartX=41.0172 StartY=-1.537e-13 StartZ=0 EndX=40.5 EndY=-1.537e-13 EndZ=0
    g3: LineSegment [constr] StartX=41.5 StartY=-1.537e-13 StartZ=0 EndX=41.5 EndY=-2 EndZ=0
    g4: LineSegment [constr] StartX=40.5 StartY=-1 StartZ=0 EndX=41.5 EndY=-1 EndZ=0
    g5: ArcOfCircle CenterX=41.0172 CenterY=-0.2 CenterZ=0 NormalX=0 NormalY=0 NormalZ=1 AngleXU=0 Radius=0.2 StartAngle=5.49779 EndAngle=7.85398
    g6: GeomPoint [constr] X=41.5 Y=-1.537e-13 Z=0
    g7: ArcOfCircle CenterX=40.7828 CenterY=-1 CenterZ=0 NormalX=0 NormalY=0 NormalZ=1 AngleXU=0 Radius=0.2 StartAngle=2.35619 EndAngle=3.92699
    g8: GeomPoint [constr] X=40.5 Y=-1 Z=0
    g9: LineSegment StartX=40.5 StartY=-1.537e-13 StartZ=0 EndX=40.5 EndY=1 EndZ=0
    g10: LineSegment StartX=40.5 StartY=1 StartZ=0 EndX=43.5 EndY=1 EndZ=0
    g11: LineSegment StartX=43.5 StartY=1 StartZ=0 EndX=43.5 EndY=-2 EndZ=0
    g12: LineSegment StartX=41.5 StartY=-2 StartZ=0 EndX=43.5 EndY=-2 EndZ=0
  constraints (33):
    c: Horizontal(g2)
    c: Perpendicular(g0,g1)
    c: Coincident(g3,g6)
    c: Vertical(g3)
    c: Coincident(g4,g8)
    c: Symmetric(g3,g3,g4)
    c: Horizontal(g4)
    c: PointOnObject(g6,g2)
    c: PointOnObject(g6,g1)
    c: Tangent(g2,g5) = -1.5708
    c: Tangent(g1,g5) = -1.5708
    c: Radius(g5) = 0.2
    c: PointOnObject(g8,g0)
    c: PointOnObject(g8,g1)
    c: Tangent(g0,g7) = 1.5708
    c: Tangent(g1,g7) = 1.5708
    c: Radius(g7) = 0.2
    c: DistanceY(g0,g2) = 2
    c: Coincident(g3,g0)
    c: DistanceX(g2,g0) = 1
    c: DistanceX(g0,g-3) = 1
    c: DistanceY(g0,g-3) = 2
    c: Distance(g9) = 1
    c: Coincident(g9,g2)
    c: Vertical(g9)
    c: Distance(g10) = 3
    c: Coincident(g10,g9)
    c: Horizontal(g10)
    c: Coincident(g11,g10)
    c: Vertical(g11)
    c: Coincident(g12,g0)
    c: Coincident(g12,g11)
    c: Horizontal(g12)
FEATURE [PartDesign::SubtractivePipe] SubtractivePipe  label="Front_Snapfit"
  AuxilleryCurvelinear = true
  AuxillerySpineTangent = false
  BaseFeature = -> Pad014
  Binormal = (0,0,0)
  Mode = 0
  Placement = pos=(0,0,0) rot=(1,1,1;2.0944rad)
  Profile = -> Sketch040
  Refine = true
  Spine = -> Pad014 [Edge159,Edge244,Edge245,Edge246]
  SpineTangent = false
  Suppressed = false
  Transformation = 0
  Transition = 2
FEATURE [Sketcher::SketchObject] Sketch044
  ArcFitTolerance = 1e-06
  AttachmentSupport = -> [SubtractivePipe]
  ExternalGeometry = -> [SubtractivePipe]
  FullyConstrained = true
  MakeInternals = false
  MapMode = 5
  Placement = pos=(9.4e-15,42.5,0) rot=(0.57735,0.57735,0.57735;4.18879rad)
  sketch-geometry (13):
    g0: LineSegment StartX=53.5172 StartY=-86 StartZ=0 EndX=53 EndY=-86 EndZ=0
    g1: LineSegment [constr] StartX=54 StartY=-86 StartZ=0 EndX=54 EndY=-84 EndZ=0
    g2: LineSegment StartX=53.6586 StartY=-85.6586 StartZ=0 EndX=53.1414 EndY=-85.1414 EndZ=0
    g3: LineSegment StartX=53.1414 StartY=-84.8586 StartZ=0 EndX=54 EndY=-84 EndZ=0
    g4: LineSegment [constr] StartX=53 StartY=-85 StartZ=0 EndX=54 EndY=-85 EndZ=0
    g5: LineSegment StartX=54 StartY=-84 StartZ=0 EndX=56 EndY=-84 EndZ=0
    g6: LineSegment StartX=56 StartY=-84 StartZ=0 EndX=56 EndY=-87 EndZ=0
    g7: LineSegment StartX=56 StartY=-87 StartZ=0 EndX=53 EndY=-87 EndZ=0
    g8: LineSegment StartX=53 StartY=-87 StartZ=0 EndX=53 EndY=-86 EndZ=0
    g9: ArcOfCircle CenterX=53.5172 CenterY=-85.8 CenterZ=0 NormalX=0 NormalY=0 NormalZ=1 AngleXU=0 Radius=0.2 StartAngle=4.71239 EndAngle=7.06858
    g10: GeomPoint [constr] X=54 Y=-86 Z=0
    g11: ArcOfCircle CenterX=53.2828 CenterY=-85 CenterZ=0 NormalX=0 NormalY=0 NormalZ=1 AngleXU=0 Radius=0.2 StartAngle=2.35619 EndAngle=3.92699
    g12: GeomPoint [constr] X=53 Y=-85 Z=0
  constraints (33):
    c: PointOnObject(g10,g-3)
    c: PointOnObject(g0,g-3)
    c: DistanceX(g0,g-3) = 2
    c: DistanceX(g0,g10) = 1
    c: Distance(g1) = 2
    c: Coincident(g1,g10)
    c: Vertical(g1)
    c: Coincident(g3,g1)
    c: Perpendicular(g2,g3)
    c: Coincident(g4,g12)
    c: Symmetric(g1,g1,g4)
    c: Horizontal(g4)
    c: Distance(g5) = 2
    c: Coincident(g5,g1)
    c: Horizontal(g5)
    c: Distance(g6) = 3
    c: Coincident(g6,g5)
    c: Vertical(g6)
    c: Coincident(g7,g6)
    c: Horizontal(g7)
    c: Coincident(g8,g7)
    c: Coincident(g8,g0)
    c: Vertical(g8)
    c: PointOnObject(g10,g2)
    c: PointOnObject(g10,g0)
    c: Tangent(g2,g9) = -1.5708
    c: Tangent(g0,g9) = 1.5708
    c: Radius(g9) = 0.2
    c: PointOnObject(g12,g2)
    c: PointOnObject(g12,g3)
    c: Tangent(g2,g11) = 1.5708
    c: Tangent(g3,g11) = 1.5708
    c: Radius(g11) = 0.2
FEATURE [PartDesign::SubtractivePipe] SubtractivePipe001  label="Rear_Snapfit"
  AuxilleryCurvelinear = true
  AuxillerySpineTangent = false
  BaseFeature = -> SubtractivePipe
  Binormal = (0,0,0)
  Mode = 0
  Placement = pos=(0,0,0) rot=(1,1,1;2.0944rad)
  Profile = -> Sketch044
  Refine = true
  Spine = -> SubtractivePipe [Edge205,Edge159,Edge206,Edge208,Edge155]
  SpineTangent = false
  Suppressed = false
  Transformation = 0
  Transition = 2
FEATURE [PartDesign::Body] Body003  label="Body"
  AllowCompound = false
  Group = -> [Sketch011,Pad006,Sketch012,Pocket005,Sketch013,Pocket006,Sketch016,Pocket008,Sketch017,Pocket009,Sketch018,Pocket010,Sketch019,Sketch020,Pocket012,Pad008,Sketch022,Pad009,Sketch023,Pocket013,Sketch024,Pocket014,Sketch025,Pad010,Sketch026,Pad011,Sketch028,Pad012,Sketch029,Pad013,Fillet013,Fillet014,Fillet015,Fillet016,Sketch030,Pad014,Sketch040,SubtractivePipe,Sketch044,SubtractivePipe001,+1 more]
  Origin = -> Origin005
  Tip = -> Fillet027
COMPONENT P3 — recipe-attached ("Drum001", modeled in this document).
Construction recipe (the document's own serialized feature program — sketch geometry with constraints, then the solid features built on it; lengths are millimeters unless a unit is written):

FEATURE [Sketcher::SketchObject] Sketch008
  ArcFitTolerance = 1e-06
  AttachmentSupport = -> [YZ_Plane002]
  FullyConstrained = true
  MakeInternals = false
  MapMode = 5
  Placement = pos=(0,0,0) rot=(0.57735,0.57735,0.57735;2.0944rad)
  sketch-geometry (1):
    g0: Circle CenterX=-12.5 CenterY=0 CenterZ=0 NormalX=0 NormalY=0 NormalZ=1 AngleXU=0 Radius=42.5
  constraints (3):
    c: PointOnObject(g0,g-1)
    c: DistanceX(g0,g-1) = 12.5
    c: Diameter(g0) = 85
FEATURE [PartDesign::Pad] Pad005  label="Drum_Depth"
  Direction = (1,0,0)
  Length = 56
  Length2 = 10
  Placement = pos=(0,0,0) rot=(1,1,1;2.0944rad)
  Profile = -> Sketch008
  ReferenceAxis = -> Sketch008 [N_Axis]
  Refine = true
  Reversed = true
  Suppressed = false
  Type = 0
FEATURE [Sketcher::SketchObject] Sketch009
  ArcFitTolerance = 1e-06
  AttachmentSupport = -> [Pad005]
  ExternalGeometry = -> [Pad005]
  FullyConstrained = true
  MakeInternals = false
  MapMode = 5
  Placement = pos=(0,0,0) rot=(0.57735,0.57735,0.57735;2.0944rad)
  expr: Constraints[44] = 31.5 / 2
  sketch-geometry (16):
    g0: ArcOfCircle CenterX=-12.5 CenterY=0 CenterZ=0 NormalX=0 NormalY=0 NormalZ=1 AngleXU=0 Radius=37.5 StartAngle=4.34412 EndAngle=5.08066
    g1: LineSegment StartX=-26 StartY=34.9857 StartZ=0 EndX=-26 EndY=14.254 EndZ=0
    g2: LineSegment StartX=1 StartY=34.9857 StartZ=0 EndX=1 EndY=14.254 EndZ=0
    g3: LineSegment [constr] StartX=-26 StartY=34.9857 StartZ=0 EndX=1 EndY=34.9857 EndZ=0
    g4: LineSegment [constr] StartX=-26 StartY=-34.9857 StartZ=0 EndX=1 EndY=-34.9857 EndZ=0
    g5: ArcOfCircle CenterX=-12.5 CenterY=0 CenterZ=0 NormalX=0 NormalY=0 NormalZ=1 AngleXU=0 Radius=37.5 StartAngle=1.20253 EndAngle=1.93906
    g6: LineSegment StartX=-26 StartY=14.254 StartZ=0 EndX=-32 EndY=15.75 EndZ=0
    g7: LineSegment StartX=-32 StartY=15.75 StartZ=0 EndX=-32 EndY=-15.75 EndZ=0
    g8: LineSegment StartX=-32 StartY=-15.75 StartZ=0 EndX=-26 EndY=-14.254 EndZ=0
    g9: LineSegment StartX=1 StartY=14.254 StartZ=0 EndX=7 EndY=15.75 EndZ=0
    g10: LineSegment StartX=7 StartY=15.75 StartZ=0 EndX=7 EndY=-15.75 EndZ=0
    g11: LineSegment StartX=7 StartY=-15.75 StartZ=0 EndX=1 EndY=-14.254 EndZ=0
    g12: LineSegment StartX=-26 StartY=-14.254 StartZ=0 EndX=-26 EndY=-34.9857 EndZ=0
    g13: LineSegment StartX=1 StartY=-14.254 StartZ=0 EndX=1 EndY=-34.9857 EndZ=0
    g14: LineSegment [constr] StartX=-26 StartY=14.254 StartZ=0 EndX=1 EndY=14.254 EndZ=0
    g15: LineSegment [constr] StartX=-26 StartY=-14.254 StartZ=0 EndX=1 EndY=-14.254 EndZ=0
  constraints (47):
    c: Coincident(g0,g-3)
    c: Diameter(g0) = 75
    c: Vertical(g1)
    c: PointOnObject(g2,g5)
    c: Vertical(g2)
    c: Coincident(g3,g1)
    c: Coincident(g3,g2)
    c: Horizontal(g3)
    c: Coincident(g4,g12)
    c: Coincident(g4,g13)
    c: DistanceX(g3,g3) = 27
    c: Coincident(g5,g1)
    c: Coincident(g0,g12)
    c: Equal(g0,g5)
    c: Coincident(g0,g13)
    c: PointOnObject(g5,g2)
    c: Coincident(g0,g5)
    c: Coincident(g7,g6)
    c: Vertical(g7)
    c: Coincident(g8,g7)
    c: PointOnObject(g8,g12)
    c: Angle(g6,g1) = 1.81514
    c: Angle(g1,g8) = 1.81514
    c: Coincident(g10,g9)
    c: Vertical(g10)
    c: Coincident(g11,g10)
    c: PointOnObject(g11,g13)
    c: Coincident(g1,g6)
    c: PointOnObject(g12,g8)
    c: Coincident(g2,g9)
    c: PointOnObject(g13,g11)
    c: Angle(g11,g13) = 1.81514
    c: Angle(g2,g9) = 1.81514
    c: Coincident(g14,g1)
    c: Coincident(g14,g2)
    c: Horizontal(g14)
    c: Coincident(g15,g8)
    c: Coincident(g15,g11)
    c: Horizontal(g15)
    c: DistanceX(g4,g4) = 27
    c: Vertical(g13)
    c: Vertical(g12)
    c: DistanceX(g2,g9) = 6
    c: DistanceY(g7,g7) = 31.5
    c: DistanceY(g0,g6) = 15.75
    c: DistanceX(g7,g12) = 6
    c: DistanceX(g6,g1) = 6
FEATURE [PartDesign::Pocket] Pocket003  label="Press_Stand"
  BaseFeature = -> Pad005
  Direction = (-1,0,0)
  Length = 35
  Length2 = 5
  Placement = pos=(0,0,0) rot=(1,1,1;2.0944rad)
  Profile = -> Sketch009
  ReferenceAxis = -> Sketch009 [N_Axis]
  Refine = true
  Suppressed = false
  Type = 0
FEATURE [Sketcher::SketchObject] Sketch010
  ArcFitTolerance = 1e-06
  AttachmentSupport = -> [Pocket003]
  ExternalGeometry = -> [Pocket003]
  FullyConstrained = true
  MakeInternals = false
  MapMode = 5
  Placement = pos=(-35,0,0) rot=(0.57735,0.57735,0.57735;2.0944rad)
  sketch-geometry (4):
    g0: ArcOfCircle CenterX=-12.5 CenterY=1.22e-14 CenterZ=0 NormalX=0 NormalY=0 NormalZ=1 AngleXU=0 Radius=37.5 StartAngle=4.34412 EndAngle=5.08066
    g1: LineSegment StartX=-26 StartY=34.9857 StartZ=0 EndX=-26 EndY=-34.9857 EndZ=0
    g2: LineSegment StartX=1 StartY=34.9857 StartZ=0 EndX=1 EndY=-34.9857 EndZ=0
    g3: ArcOfCircle CenterX=-12.5 CenterY=1.22e-14 CenterZ=0 NormalX=0 NormalY=0 NormalZ=1 AngleXU=0 Radius=37.5 StartAngle=1.20253 EndAngle=1.93906
  constraints (11):
    c: Coincident(g0,g-3)
    c: Coincident(g1,g-3)
    c: Vertical(g1)
    c: Coincident(g2,g-3)
    c: Vertical(g2)
    c: Coincident(g3,g1)
    c: Coincident(g0,g1)
    c: Equal(g0,g3)
    c: Coincident(g0,g2)
    c: PointOnObject(g3,g2)
    c: Coincident(g0,g3)
FEATURE [PartDesign::Pocket] Pocket004  label="Press_Depth"
  BaseFeature = -> Pocket003
  Direction = (-1,0,0)
  Length = 19
  Length2 = 5
  Placement = pos=(0,0,0) rot=(1,1,1;2.0944rad)
  Profile = -> Sketch010
  ReferenceAxis = -> Sketch010 [N_Axis]
  Refine = true
  Suppressed = false
  Type = 0
FEATURE [Sketcher::SketchObject] Sketch014
  ArcFitTolerance = 1e-06
  AttachmentSupport = -> [Pocket004]
  ExternalGeometry = -> [Pocket004]
  FullyConstrained = true
  MakeInternals = false
  MapMode = 5
  Placement = pos=(-56,0,0) rot=(0.57735,0.57735,-0.57735;4.18879rad)
  sketch-geometry (1):
    g0: Circle CenterX=-12.5 CenterY=0 CenterZ=0 NormalX=0 NormalY=0 NormalZ=1 AngleXU=0 Radius=10
  constraints (2):
    c: Coincident(g0,g-3)
    c: Diameter(g0) = 20
FEATURE [PartDesign::Pad] Pad007  label="Motor_Pad"
  BaseFeature = -> Pocket004
  Direction = (-1,0,0)
  Length = 6
  Length2 = 10
  Placement = pos=(0,0,0) rot=(1,1,1;2.0944rad)
  Profile = -> Sketch014
  ReferenceAxis = -> Sketch014 [N_Axis]
  Refine = true
  Suppressed = false
  Type = 0
FEATURE [Sketcher::SketchObject] Sketch015
  ArcFitTolerance = 1e-06
  AttachmentSupport = -> [Pad007]
  ExternalGeometry = -> [Pad007]
  FullyConstrained = true
  MakeInternals = false
  MapMode = 5
  Placement = pos=(-62,0,0) rot=(0.57735,0.57735,-0.57735;4.18879rad)
  sketch-geometry (5):
    g0: ArcOfCircle CenterX=-12.5 CenterY=1.52e-14 CenterZ=0 NormalX=0 NormalY=0 NormalZ=1 AngleXU=0 Radius=2.55 StartAngle=0.917455 EndAngle=2.22414
    g1: LineSegment [constr] StartX=-10.95 StartY=-2.02485 StartZ=0 EndX=-14.05 EndY=-2.02485 EndZ=0
    g2: LineSegment StartX=-10.95 StartY=-2.02485 StartZ=0 EndX=-10.95 EndY=2.02485 EndZ=0
    g3: LineSegment StartX=-14.05 StartY=-2.02485 StartZ=0 EndX=-14.05 EndY=2.02485 EndZ=0
    g4: ArcOfCircle CenterX=-12.5 CenterY=1.52e-14 CenterZ=0 NormalX=0 NormalY=0 NormalZ=1 AngleXU=0 Radius=2.55 StartAngle=4.05905 EndAngle=5.36573
  constraints (15):
    c: Coincident(g0,g-3)
    c: Diameter(g0) = 5.1
    c: PointOnObject(g1,g4)
    c: Horizontal(g1)
    c: Coincident(g2,g1)
    c: Vertical(g2)
    c: Coincident(g3,g1)
    c: Vertical(g3)
    c: DistanceX(g1,g1) = 3.1
    c: Coincident(g4,g2)
    c: Coincident(g0,g2)
    c: Equal(g0,g4)
    c: Coincident(g0,g3)
    c: PointOnObject(g4,g3)
    c: Coincident(g0,g4)
FEATURE [PartDesign::Pocket] Pocket007  label="Motor_Axis"
  BaseFeature = -> Pad007
  Direction = (1,0,0)
  Length = 6
  Length2 = 5
  Placement = pos=(0,0,0) rot=(1,1,1;2.0944rad)
  Profile = -> Sketch015
  ReferenceAxis = -> Sketch015 [N_Axis]
  Refine = true
  Suppressed = false
  Type = 0
FEATURE [PartDesign::Fillet] Fillet010
  Base = -> Pocket007 [Edge32,Edge34,Edge33,Edge36,Edge38,Edge20,Edge21,Edge25,Edge27,Edge22]
  BaseFeature = -> Pocket007
  Placement = pos=(0,0,0) rot=(1,1,1;2.0944rad)
  Radius = 1
  Refine = true
  SupportTransform = false
  Suppressed = false
  UseAllEdges = false
FEATURE [PartDesign::Fillet] Fillet011
  Base = -> Fillet010 [Edge70]
  BaseFeature = -> Fillet010
  Placement = pos=(0,0,0) rot=(1,1,1;2.0944rad)
  Radius = 2
  Refine = true
  SupportTransform = false
  Suppressed = false
  UseAllEdges = false
FEATURE [Sketcher::SketchObject] Sketch034
  ArcFitTolerance = 1e-06
  AttachmentSupport = -> [Fillet011]
  ExternalGeometry = -> [Fillet011]
  FullyConstrained = false
  MakeInternals = false
  MapMode = 5
  Placement = pos=(-7e-15,-32,0) rot=(0.57735,0.57735,0.57735;4.18879rad)
  sketch-geometry (5):
    g0: LineSegment StartX=-17.929 StartY=-13 StartZ=0 EndX=-17.929 EndY=-16 EndZ=0
    g1: LineSegment StartX=-17.929 StartY=-16 StartZ=0 EndX=17.929 EndY=-16 EndZ=0
    g2: LineSegment StartX=17.929 StartY=-16 StartZ=0 EndX=17.929 EndY=-13 EndZ=0
    g3: LineSegment StartX=17.929 StartY=-13 StartZ=0 EndX=-17.929 EndY=-13 EndZ=0
    g4: LineSegment [constr] StartX=1.3289e-12 StartY=-13 StartZ=0 EndX=1.3289e-12 EndY=-35 EndZ=0
  constraints (13):
    c: Coincident(g0,g1)
    c: Coincident(g1,g2)
    c: Coincident(g2,g3)
    c: Coincident(g3,g0)
    c: Vertical(g0)
    c: Vertical(g2)
    c: Horizontal(g1)
    c: Horizontal(g3)
    c: DistanceY(g0,g0) = 3
    c: DistanceY(g-3,g0) = 19
    c: Symmetric(g3,g3,g4)
    c: Symmetric(g-3,g-3,g4)
    c: Vertical(g4)
FEATURE [PartDesign::Pad] Pad017  label="Press_Dovetail_Stopper_R"
  BaseFeature = -> Fillet011
  Direction = (-1e-16,1,-1e-15)
  Length = 0.5
  Length2 = 10
  Placement = pos=(0,0,0) rot=(1,1,1;2.0944rad)
  Profile = -> Sketch034
  ReferenceAxis = -> Sketch034 [N_Axis]
  Refine = true
  Suppressed = false
  Type = 0
FEATURE [Sketcher::SketchObject] Sketch035
  ArcFitTolerance = 1e-06
  AttachmentSupport = -> [Pad017]
  ExternalGeometry = -> [Pad017]
  FullyConstrained = false
  MakeInternals = false
  MapMode = 5
  Placement = pos=(1.5e-15,7,0) rot=(0.57735,0.57735,-0.57735;2.0944rad)
  sketch-geometry (5):
    g0: LineSegment StartX=-16.6626 StartY=-13 StartZ=0 EndX=-16.6626 EndY=-16 EndZ=0
    g1: LineSegment StartX=-16.6626 StartY=-16 StartZ=0 EndX=16.6626 EndY=-16 EndZ=0
    g2: LineSegment StartX=16.6626 StartY=-16 StartZ=0 EndX=16.6626 EndY=-13 EndZ=0
    g3: LineSegment StartX=16.6626 StartY=-13 StartZ=0 EndX=-16.6626 EndY=-13 EndZ=0
    g4: LineSegment [constr] StartX=-6.5215e-12 StartY=-16 StartZ=0 EndX=-6.5215e-12 EndY=-35 EndZ=0
  constraints (13):
    c: Coincident(g0,g1)
    c: Coincident(g1,g2)
    c: Coincident(g2,g3)
    c: Coincident(g3,g0)
    c: Vertical(g0)
    c: Vertical(g2)
    c: Horizontal(g1)
    c: Horizontal(g3)
    c: DistanceY(g0,g0) = 3
    c: Symmetric(g1,g1,g4)
    c: Symmetric(g-3,g-3,g4)
    c: Vertical(g4)
    c: DistanceY(g-3,g0) = 19
FEATURE [PartDesign::Pad] Pad018  label="Press_Dovetail_Stopper_L"
  BaseFeature = -> Pad017
  Direction = (0,-1,1.3e-15)
  Length = 0.5
  Length2 = 10
  Placement = pos=(0,0,0) rot=(1,1,1;2.0944rad)
  Profile = -> Sketch035
  ReferenceAxis = -> Sketch035 [N_Axis]
  Refine = true
  Suppressed = false
  Type = 0
FEATURE [PartDesign::Fillet] Fillet017
  Base = -> Pad018 [Edge79,Edge61,Edge104,Edge110]
  BaseFeature = -> Pad018
  Placement = pos=(0,0,0) rot=(1,1,1;2.0944rad)
  Radius = 0.2
  Refine = true
  SupportTransform = false
  Suppressed = false
  UseAllEdges = false
FEATURE [PartDesign::Fillet] Fillet018
  Base = -> Fillet017 [Edge23,Edge30,Edge120,Edge116]
  BaseFeature = -> Fillet017
  Placement = pos=(0,0,0) rot=(1,1,1;2.0944rad)
  Radius = 0.25
  Refine = true
  SupportTransform = false
  Suppressed = false
  UseAllEdges = false
FEATURE [PartDesign::Fillet] Fillet019
  Base = -> Fillet018 [Edge120]
  BaseFeature = -> Fillet018
  Placement = pos=(0,0,0) rot=(1,1,1;2.0944rad)
  Radius = 2
  Refine = true
  SupportTransform = false
  Suppressed = false
  UseAllEdges = false
FEATURE [PartDesign::Body] Body002  label="Drum"
  AllowCompound = false
  Group = -> [Sketch008,Pad005,Sketch009,Pocket003,Sketch010,Pocket004,Sketch014,Pad007,Sketch015,Pocket007,Fillet010,Fillet011,Sketch034,Pad017,Sketch035,Pad018,Fillet017,Fillet018,Fillet019]
  Origin = -> Origin002
  Tip = -> Fillet019
COMPONENT P4 — geometry summary ("L Bolt M4 x 15 Stainless Steel001"; no construction recipe available for this part):
  bounding box: 19.0 x 7.0 x 7.0 mm
  tessellated surface: 6,816 triangles
  volume: 320 mm^3 (34% of its bounding box)
  symmetry: revolution-symmetric about the x axis through its bounding-box center; mirror-symmetric across its y mid-plane
COMPONENT P5 — geometry summary ("L Bolt M4 x 15 Stainless Steel002"; no construction recipe available for this part):
  bounding box: 19.0 x 7.0 x 7.0 mm
  tessellated surface: 6,816 triangles
  volume: 320 mm^3 (34% of its bounding box)
  symmetry: revolution-symmetric about the x axis through its bounding-box center; mirror-symmetric across its y mid-plane
COMPONENT P6 — geometry summary ("M3 insert nut brass001"; no construction recipe available for this part):
  bounding box: 4.5 x 4.5 x 4.0 mm
  tessellated surface: 10,262 triangles
  volume: 27 mm^3 (33% of its bounding box)
COMPONENT P7 — geometry summary ("M3 insert nut brass002"; no construction recipe available for this part):
  bounding box: 4.5 x 4.5 x 4.0 mm
  tessellated surface: 10,262 triangles
  volume: 27 mm^3 (33% of its bounding box)
COMPONENT P8 — geometry summary ("M3x8 Philips Screw001"; no construction recipe available for this part):
  bounding box: 9.8 x 5.3 x 5.3 mm
  tessellated surface: 28,998 triangles
  volume: 69 mm^3 (25% of its bounding box)
COMPONENT P9 — geometry summary ("M3x8 Philips Screw002"; no construction recipe available for this part):
  bounding box: 9.8 x 5.3 x 5.3 mm
  tessellated surface: 28,998 triangles
  volume: 69 mm^3 (25% of its bounding box)
COMPONENT P10 — geometry summary ("M4x6mm_threaded_brass_insert001"; no construction recipe available for this part):
  bounding box: 6.0 x 5.2 x 5.2 mm
  tessellated surface: 11,232 triangles
  volume: 49 mm^3 (30% of its bounding box)
COMPONENT P11 — geometry summary ("M4x6mm_threaded_brass_insert002"; no construction recipe available for this part):
  bounding box: 6.0 x 5.2 x 5.2 mm
  tessellated surface: 11,232 triangles
  volume: 49 mm^3 (30% of its bounding box)
COMPONENT P12 — geometry summary ("608zz001"; no construction recipe available for this part):
  bounding box: 22.0 x 22.0 x 7.0 mm
  tessellated surface: 109,956 triangles
  volume: 1836 mm^3 (54% of its bounding box)
  symmetry: 2-fold rotationally symmetric about the z axis; mirror-symmetric across its x mid-plane, y mid-plane
COMPONENT P13 — geometry summary ("608zz002"; no construction recipe available for this part):
  bounding box: 22.0 x 22.0 x 7.0 mm
  tessellated surface: 109,956 triangles
  volume: 1836 mm^3 (54% of its bounding box)
  symmetry: 2-fold rotationally symmetric about the z axis; mirror-symmetric across its x mid-plane, y mid-plane
PROVENANCE & LICENSES
A FreeCAD (.FCStd) document from a public repository crawl; recipes are the document's own serialized feature recipes (and, for linked parts, companion documents' recipes).
License: gpl-3.0.
